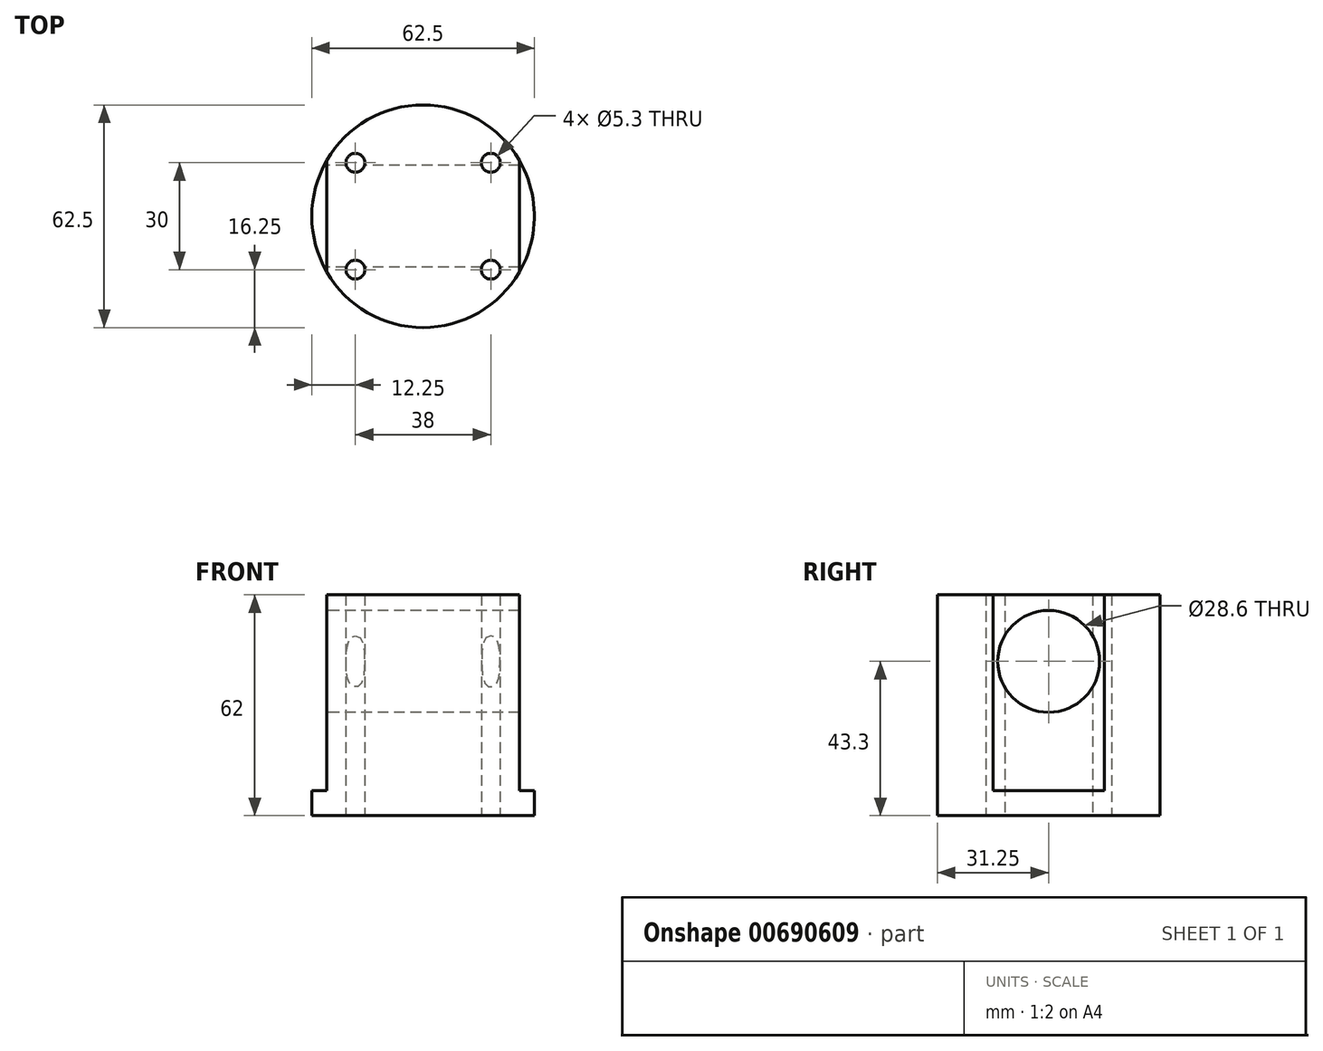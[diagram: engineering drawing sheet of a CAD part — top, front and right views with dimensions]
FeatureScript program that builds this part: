
annotation { "Feature Type Name" : "Feature", "Feature Type Description" : "" }
export const myFeature = defineFeature(function(context is Context, id is Id, definition is map)
    precondition{}
    {
        {
            var Q0;
            Q0=qCreatedBy(makeId("Top.planeOp"),FACE);
            var sketch = newSketch(context, id + "F0", { "sketchPlane" : qUnion([Q0])});
            skCircle(sketch, "E0", {"center": v(0, 0) * mm, "radius": 31.25 * mm});
            skCircle(sketch, "E1", {"center": v(-19, 15) * mm, "radius": 2.65 * mm});
            skCircle(sketch, "E2", {"center": v(-19, -15) * mm, "radius": 2.65 * mm});
            skCircle(sketch, "E3", {"center": v(19, -15) * mm, "radius": 2.65 * mm});
            skCircle(sketch, "E4", {"center": v(19, 15) * mm, "radius": 2.65 * mm});
            skSolve(sketch);
        }
        {
            var Q0;
            Q0=makeQuery(id+"F0.imprint","IMPRINT",FACE,{"disambiguationData":[TD([[makeQuery(id+"F0.imprint","IMPRINT",EDGE,{"derivedFrom":sQuery(id+"F0.wireOp",EDGE,"E0")}),1.0]])]});
            extrude(context, id + "F1", {"entities" : qUnion([Q0]), "depth" : 62 * mm, "offsetDistance" : 25 * mm});
        }
        {
            var Q0;
            Q0=makeQuery(id+"F1.opExtrude","CAP_FACE",FACE,{"disambiguationData":[OSD([sQuery(id+"F0.wireOp",EDGE,"E0"),sQuery(id+"F0.wireOp",EDGE,"E1"),sQuery(id+"F0.wireOp",EDGE,"E2"),sQuery(id+"F0.wireOp",EDGE,"E3"),sQuery(id+"F0.wireOp",EDGE,"E4")])],"isStart":false});
            var sketch = newSketch(context, id + "F2", { "sketchPlane" : qUnion([Q0])});
            skLineSegment(sketch, "E5.left", {"start": v(-27.05, 15.65) * mm, "end": v(-27.05, -15.65) * mm});
            skLineSegment(sketch, "E5.right", {"start": v(27.05, 15.65) * mm, "end": v(27.05, -15.65) * mm});
            skPoint(sketch, "E5.middle", {"position": v(0, 0) * mm});
            skArc(sketch, "E6", {"start": v(-27.05, 15.65) * mm, "mid": v(-31.26, 0) * mm, "end": v(-27.05, -15.65) * mm});
            skArc(sketch, "E7", {"start": v(27.05, -15.65) * mm, "mid": v(31.25, 0) * mm, "end": v(27.05, 15.65) * mm});
            skPoint(sketch, "E5.bottom.start.orphan", {"position": v(-27.05, 28.64) * mm});
            skPoint(sketch, "E8.orphan", {"position": v(27.05, 28.64) * mm});
            skPoint(sketch, "E5.top.end.orphan", {"position": v(27.05, -28.64) * mm});
            skPoint(sketch, "E9.orphan", {"position": v(-27.05, -28.64) * mm});
            skSolve(sketch);
        }
        {
            var Q0;
            {var subQ0=sQuery(id+"F2.wireOp",EDGE,"E5.left");Q0=makeQuery(id+"F2.imprint","IMPRINT",FACE,{"disambiguationData":[TD([[makeQuery(id+"F2.imprint","IMPRINT",EDGE,{"derivedFrom":subQ0}),-1.0]])]});}
            var Q1;
            Q1=makeQuery(id+"F2.imprint","IMPRINT",FACE,{"disambiguationData":[TD([[makeQuery(id+"F2.imprint","IMPRINT",EDGE,{"derivedFrom":sQuery(id+"F2.wireOp",EDGE,"E5.right")}),1.0]])]});
            extrude(context, id + "F3", {"entities" : qUnion([Q0, Q1]), "operationType" : NewBodyOperationType.REMOVE, "oppositeDirection" : true, "depth" : 55 * mm, "offsetDistance" : 25 * mm});
        }
        {
            var Q0;
            Q0=makeQuery(id+"F3.boolean.opBoolean","COPY",FACE,{"derivedFrom":makeQuery(id+"F3.opExtrude","SWEPT_FACE",FACE,{"disambiguationData":[OSD([sQuery(id+"F2.wireOp",EDGE,"E5.left")])]})});
            var sketch = newSketch(context, id + "F4", { "sketchPlane" : qUnion([Q0])});
            skCircle(sketch, "E10", {"center": v(0, 43.3) * mm, "radius": 14.3 * mm});
            skSolve(sketch);
        }
        {
            var Q0;
            Q0=makeQuery(id+"F4.imprint","IMPRINT",FACE,{"disambiguationData":[TD([[makeQuery(id+"F4.imprint","IMPRINT",EDGE,{"derivedFrom":sQuery(id+"F4.wireOp",EDGE,"E10")}),1.0]])]});
            extrude(context, id + "F5", {"entities" : qUnion([Q0]), "operationType" : NewBodyOperationType.REMOVE, "endBound" : BoundingType.THROUGH_ALL, "oppositeDirection" : true, "depth" : 25 * mm, "offsetDistance" : 25 * mm});
        }
    });
